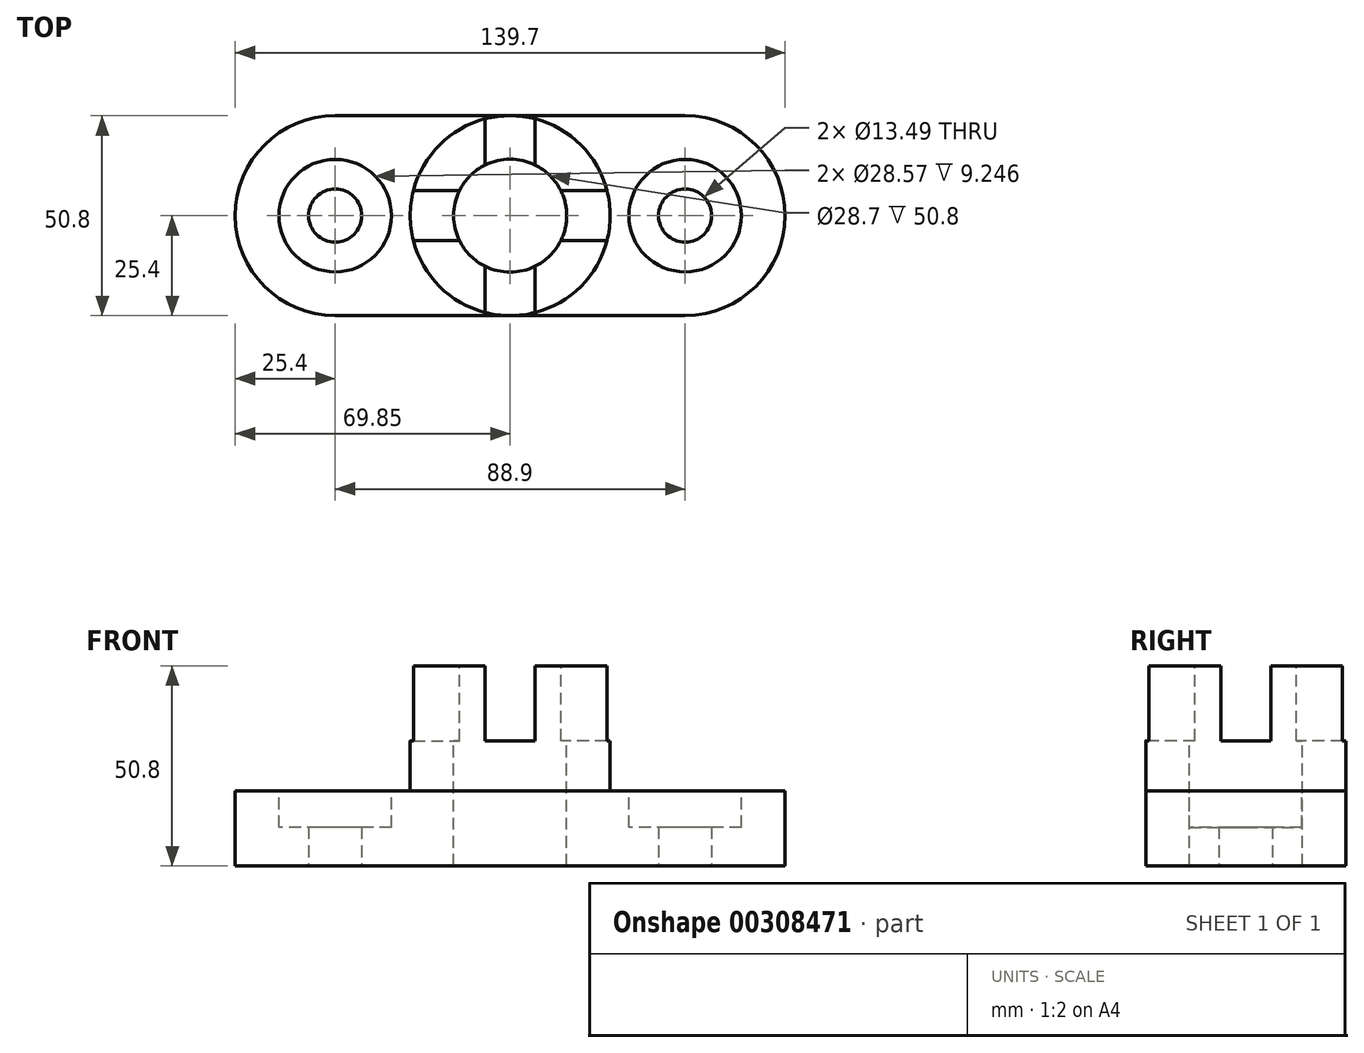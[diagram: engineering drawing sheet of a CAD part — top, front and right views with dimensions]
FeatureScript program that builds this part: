
annotation { "Feature Type Name" : "Feature", "Feature Type Description" : "" }
export const myFeature = defineFeature(function(context is Context, id is Id, definition is map)
    precondition{}
    {
        {
            var Q0;
            Q0=qCreatedBy(makeId("Top.planeOp"),FACE);
            var sketch = newSketch(context, id + "F0", { "sketchPlane" : qUnion([Q0])});
            skLineSegment(sketch, "E0", {"start": v(0, 25.4) * mm, "end": v(88.9, 25.4) * mm});
            skLineSegment(sketch, "E1", {"start": v(0, -25.4) * mm, "end": v(88.9, -25.4) * mm});
            skCircle(sketch, "E2", {"center": v(0, 0) * mm, "radius": 6.74 * mm});
            skCircle(sketch, "E3", {"center": v(88.9, 0) * mm, "radius": 6.74 * mm});
            skArc(sketch, "E4", {"start": v(0, 25.4) * mm, "mid": v(-25.4, 0) * mm, "end": v(0, -25.4) * mm});
            skArc(sketch, "E5", {"start": v(88.9, -25.4) * mm, "mid": v(114.3, 0) * mm, "end": v(88.9, 25.4) * mm});
            skSolve(sketch);
        }
        {
            var Q0;
            Q0=makeQuery(id+"F0.imprint","IMPRINT",FACE,{"disambiguationData":[TD([[makeQuery(id+"F0.imprint","IMPRINT",EDGE,{"derivedFrom":sQuery(id+"F0.wireOp",EDGE,"E0")}),-1.0]])]});
            extrude(context, id + "F1", {"entities" : qUnion([Q0]), "depth" : 19.05 * mm});
        }
        {
            var Q0;
            Q0=makeQuery(id+"F1.opExtrude","CAP_FACE",FACE,{"disambiguationData":[OSD([sQuery(id+"F0.wireOp",EDGE,"E0"),sQuery(id+"F0.wireOp",EDGE,"E1"),sQuery(id+"F0.wireOp",EDGE,"E2"),sQuery(id+"F0.wireOp",EDGE,"E3"),sQuery(id+"F0.wireOp",EDGE,"E4"),sQuery(id+"F0.wireOp",EDGE,"E5")])],"isStart":false});
            var sketch = newSketch(context, id + "F2", { "sketchPlane" : qUnion([Q0])});
            skCircle(sketch, "E6", {"center": v(0, 0) * mm, "radius": 14.29 * mm});
            skCircle(sketch, "E7", {"center": v(88.9, 0) * mm, "radius": 14.29 * mm});
            skSolve(sketch);
        }
        {
            var Q0;
            Q0 = qSketchRegion(id + "F2", true);
            extrude(context, id + "F3", {"entities" : qUnion([Q0]), "operationType" : NewBodyOperationType.REMOVE, "oppositeDirection" : true, "depth" : 9.25 * mm});
        }
        {
            var Q0;
            Q0=makeQuery(id+"F1.opExtrude","CAP_FACE",FACE,{"disambiguationData":[OSD([sQuery(id+"F0.wireOp",EDGE,"E0"),sQuery(id+"F0.wireOp",EDGE,"E1"),sQuery(id+"F0.wireOp",EDGE,"E2"),sQuery(id+"F0.wireOp",EDGE,"E3"),sQuery(id+"F0.wireOp",EDGE,"E4"),sQuery(id+"F0.wireOp",EDGE,"E5")])],"isStart":false});
            var sketch = newSketch(context, id + "F4", { "sketchPlane" : qUnion([Q0])});
            skCircle(sketch, "E8", {"center": v(44.45, 0) * mm, "radius": 25.4 * mm});
            skSolve(sketch);
        }
        {
            var Q0;
            Q0 = qSketchRegion(id + "F4", true);
            extrude(context, id + "F5", {"entities" : qUnion([Q0]), "operationType" : NewBodyOperationType.ADD, "depth" : 31.75 * mm});
        }
        {
            var Q0;
            Q0=makeQuery(id+"F5.opExtrude","CAP_FACE",FACE,{"disambiguationData":[OSD([sQuery(id+"F4.wireOp",EDGE,"E8")])],"isStart":false});
            var sketch = newSketch(context, id + "F6", { "sketchPlane" : qUnion([Q0])});
            skCircle(sketch, "E9", {"center": v(44.45, 0) * mm, "radius": 14.35 * mm});
            skSolve(sketch);
        }
        {
            var Q0;
            Q0 = qSketchRegion(id + "F6", true);
            extrude(context, id + "F7", {"entities" : qUnion([Q0]), "operationType" : NewBodyOperationType.REMOVE, "endBound" : BoundingType.THROUGH_ALL, "oppositeDirection" : true, "depth" : 25.4 * mm});
        }
        {
            var Q0;
            Q0=makeQuery(id+"F5.opExtrude","CAP_FACE",FACE,{"disambiguationData":[OSD([sQuery(id+"F4.wireOp",EDGE,"E8")])],"isStart":false});
            var sketch = newSketch(context, id + "F8", { "sketchPlane" : qUnion([Q0])});
            skLineSegment(sketch, "E10", {"start": v(44.45, 0) * mm, "end": v(44.45, 34.37) * mm, "construction": true});
            skLineSegment(sketch, "E11", {"start": v(44.45, 0) * mm, "end": v(78.82, 0) * mm, "construction": true});
            skLineSegment(sketch, "E12", {"start": v(44.45, 0) * mm, "end": v(10.09, 0) * mm, "construction": true});
            skLineSegment(sketch, "E13", {"start": v(44.45, 0) * mm, "end": v(44.45, -34.37) * mm, "construction": true});
            skLineSegment(sketch, "E14", {"start": v(44.45, 34.37) * mm, "end": v(38.1, 34.37) * mm});
            skLineSegment(sketch, "E15", {"start": v(38.1, 34.37) * mm, "end": v(38.1, 6.35) * mm});
            skLineSegment(sketch, "E16", {"start": v(38.1, 6.35) * mm, "end": v(10.09, 6.35) * mm});
            skLineSegment(sketch, "E17", {"start": v(10.09, 6.35) * mm, "end": v(10.09, 0) * mm});
            skLineSegment(sketch, "E18", {"start": v(10.09, 0) * mm, "end": v(10.09, -6.35) * mm});
            skLineSegment(sketch, "E19", {"start": v(10.09, -6.35) * mm, "end": v(38.1, -6.35) * mm});
            skLineSegment(sketch, "E20", {"start": v(38.1, -6.35) * mm, "end": v(38.1, -34.37) * mm});
            skLineSegment(sketch, "E21", {"start": v(38.1, -34.37) * mm, "end": v(44.45, -34.37) * mm});
            skLineSegment(sketch, "E22", {"start": v(44.45, -34.37) * mm, "end": v(50.8, -34.37) * mm});
            skLineSegment(sketch, "E23", {"start": v(50.8, -34.37) * mm, "end": v(50.8, -6.35) * mm});
            skLineSegment(sketch, "E24", {"start": v(50.8, -6.35) * mm, "end": v(78.82, -6.35) * mm});
            skLineSegment(sketch, "E25", {"start": v(78.82, -6.35) * mm, "end": v(78.82, 0) * mm});
            skLineSegment(sketch, "E26", {"start": v(78.82, 0) * mm, "end": v(78.82, 6.35) * mm});
            skLineSegment(sketch, "E27", {"start": v(78.82, 6.35) * mm, "end": v(50.8, 6.35) * mm});
            skLineSegment(sketch, "E28", {"start": v(50.8, 6.35) * mm, "end": v(50.8, 34.37) * mm});
            skLineSegment(sketch, "E29", {"start": v(50.8, 34.37) * mm, "end": v(44.45, 34.37) * mm});
            skLineSegment(sketch, "E30", {"start": v(47.62, 34.37) * mm, "end": v(47.62, -34.37) * mm});
            skSolve(sketch);
        }
        {
            var Q0;
            Q0 = qSketchRegion(id + "F8", true);
            extrude(context, id + "F9", {"entities" : qUnion([Q0]), "operationType" : NewBodyOperationType.REMOVE, "oppositeDirection" : true, "depth" : 19.05 * mm});
        }
    });
